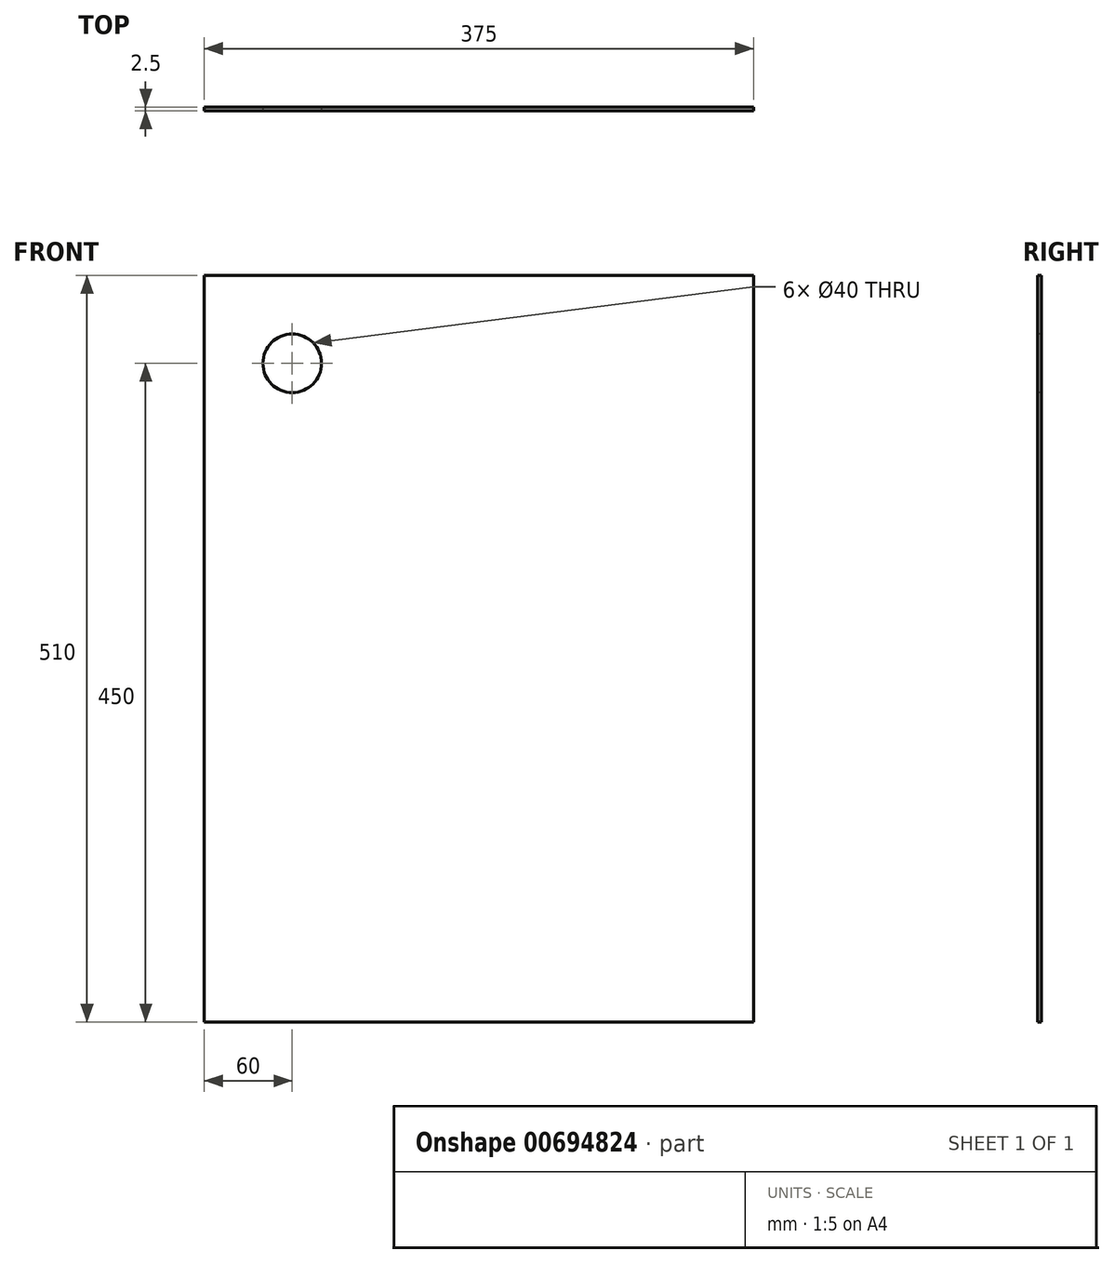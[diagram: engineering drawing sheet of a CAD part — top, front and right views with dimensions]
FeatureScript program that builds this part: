
annotation { "Feature Type Name" : "Feature", "Feature Type Description" : "" }
export const myFeature = defineFeature(function(context is Context, id is Id, definition is map)
    precondition{}
    {
        {
            var Q0;
            Q0=qCreatedBy(makeId("Front.planeOp"),FACE);
            var sketch = newSketch(context, id + "F0", { "sketchPlane" : qUnion([Q0])});
            skLineSegment(sketch, "E0.bottom", {"start": v(0, 0) * mm, "end": v(375, 0) * mm});
            skLineSegment(sketch, "E0.top", {"start": v(0, 510) * mm, "end": v(375, 510) * mm});
            skLineSegment(sketch, "E0.left", {"start": v(0, 0) * mm, "end": v(0, 510) * mm});
            skLineSegment(sketch, "E0.right", {"start": v(375, 0) * mm, "end": v(375, 510) * mm});
            skSolve(sketch);
        }
        {
            var Q0;
            Q0=qSketchRegion(id+"F0",true);
            extrude(context, id + "F1", {"entities" : qUnion([Q0]), "depth" : 2.5 * mm, "offsetDistance" : 25 * mm});
        }
        {
            var Q0;
            Q0=makeQuery(id+"F1.opExtrude","CAP_FACE",FACE,{"disambiguationData":[OSD([sQuery(id+"F0.wireOp",EDGE,"E0.bottom"),sQuery(id+"F0.wireOp",EDGE,"E0.top"),sQuery(id+"F0.wireOp",EDGE,"E0.left"),sQuery(id+"F0.wireOp",EDGE,"E0.right")])],"isStart":false});
            var sketch = newSketch(context, id + "F2", { "sketchPlane" : qUnion([Q0])});
            skCircle(sketch, "E1", {"center": v(60, 450) * mm, "radius": 20 * mm});
            skSolve(sketch);
        }
        {
            var Q0;
            Q0=makeQuery(id+"F2.imprint","IMPRINT",FACE,{"disambiguationData":[TD([[makeQuery(id+"F2.imprint","IMPRINT",EDGE,{"derivedFrom":sQuery(id+"F2.wireOp",EDGE,"E1")}),1.0]])]});
            extrude(context, id + "F3", {"entities" : qUnion([Q0]), "operationType" : NewBodyOperationType.REMOVE, "oppositeDirection" : true, "depth" : 25 * mm, "offsetDistance" : 25 * mm});
        }
    });
